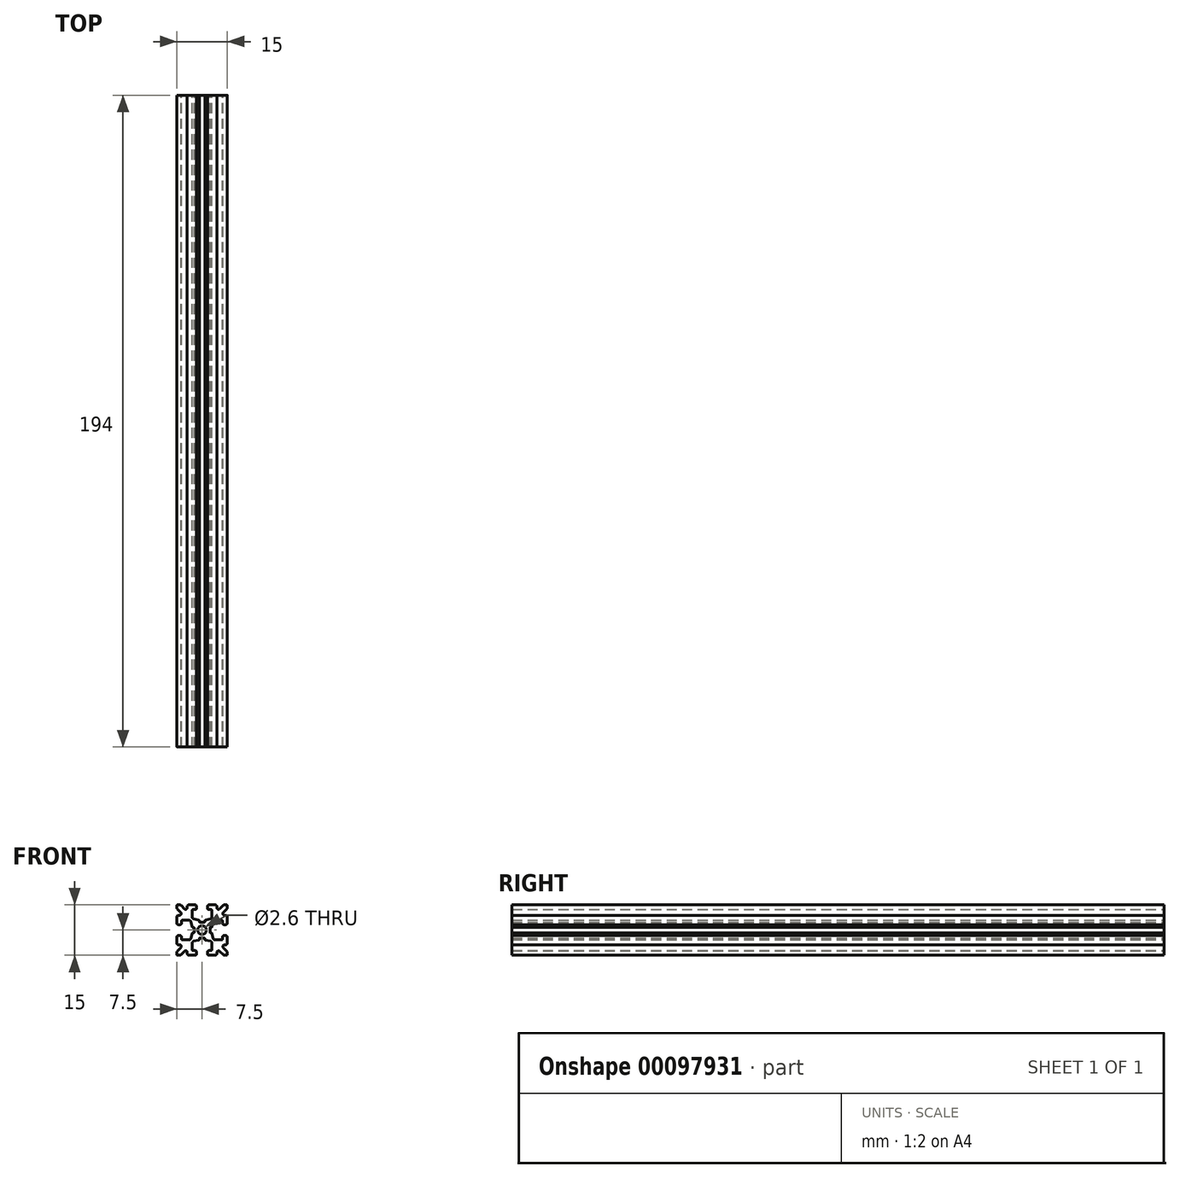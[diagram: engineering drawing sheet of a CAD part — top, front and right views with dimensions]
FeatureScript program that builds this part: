
annotation { "Feature Type Name" : "Feature", "Feature Type Description" : "" }
export const myFeature = defineFeature(function(context is Context, id is Id, definition is map)
    precondition{}
    {
        {
            var Q0;
            Q0=qCreatedBy(makeId("Front.planeOp"),FACE);
            var sketch = newSketch(context, id + "F0", { "sketchPlane" : qUnion([Q0])});
            skLineSegment(sketch, "E0.0.0", {"start": v(0.83, -2.55) * mm, "end": v(0.83, -2.77) * mm});
            skArc(sketch, "E0.0.1", {"start": v(0.83, -2.77) * mm, "mid": v(0.87, -2.9) * mm, "end": v(0.98, -2.97) * mm});
            skLineSegment(sketch, "E0.0.2", {"start": v(0.98, -2.97) * mm, "end": v(2.5, -3.31) * mm});
            skArc(sketch, "E0.0.3", {"start": v(2.5, -3.31) * mm, "mid": v(2.8, -3.49) * mm, "end": v(2.9, -3.8) * mm});
            skLineSegment(sketch, "E0.0.4", {"start": v(2.9, -3.8) * mm, "end": v(2.9, -5.9) * mm});
            skArc(sketch, "E0.0.5", {"start": v(2.9, -5.9) * mm, "mid": v(2.84, -6.04) * mm, "end": v(2.7, -6.1) * mm});
            skLineSegment(sketch, "E0.0.6", {"start": v(2.7, -6.1) * mm, "end": v(2.1, -6.1) * mm});
            skArc(sketch, "E0.0.7", {"start": v(2.1, -6.1) * mm, "mid": v(1.75, -6.25) * mm, "end": v(1.6, -6.6) * mm});
            skLineSegment(sketch, "E0.0.8", {"start": v(1.6, -6.6) * mm, "end": v(1.6, -7) * mm});
            skArc(sketch, "E0.0.9", {"start": v(1.6, -7) * mm, "mid": v(1.75, -7.35) * mm, "end": v(2.1, -7.5) * mm});
            skLineSegment(sketch, "E0.0.10", {"start": v(2.1, -7.5) * mm, "end": v(3.9, -7.5) * mm});
            skArc(sketch, "E0.0.11", {"start": v(3.9, -7.5) * mm, "mid": v(4.25, -7.35) * mm, "end": v(4.4, -7) * mm});
            skLineSegment(sketch, "E0.0.12", {"start": v(4.4, -7) * mm, "end": v(4.4, -6.67) * mm});
            skArc(sketch, "E0.0.13", {"start": v(4.4, -6.67) * mm, "mid": v(4.7, -6.2) * mm, "end": v(5.25, -6.31) * mm});
            skLineSegment(sketch, "E0.0.14", {"start": v(5.25, -6.31) * mm, "end": v(6.3, -7.35) * mm});
            skArc(sketch, "E0.0.15", {"start": v(6.3, -7.35) * mm, "mid": v(6.46, -7.46) * mm, "end": v(6.65, -7.5) * mm});
            skLineSegment(sketch, "E0.0.16", {"start": v(6.65, -7.5) * mm, "end": v(7.25, -7.5) * mm});
            skArc(sketch, "E0.0.17", {"start": v(7.25, -7.5) * mm, "mid": v(7.43, -7.43) * mm, "end": v(7.5, -7.25) * mm});
            skLineSegment(sketch, "E0.0.18", {"start": v(7.5, -7.25) * mm, "end": v(7.5, -6.65) * mm});
            skArc(sketch, "E0.0.19", {"start": v(7.5, -6.65) * mm, "mid": v(7.46, -6.46) * mm, "end": v(7.35, -6.3) * mm});
            skLineSegment(sketch, "E0.0.20", {"start": v(7.35, -6.3) * mm, "end": v(6.31, -5.25) * mm});
            skArc(sketch, "E0.0.21", {"start": v(6.31, -5.25) * mm, "mid": v(6.2, -4.7) * mm, "end": v(6.67, -4.4) * mm});
            skLineSegment(sketch, "E0.0.22", {"start": v(6.67, -4.4) * mm, "end": v(7, -4.4) * mm});
            skArc(sketch, "E0.0.23", {"start": v(7, -4.4) * mm, "mid": v(7.35, -4.25) * mm, "end": v(7.5, -3.9) * mm});
            skLineSegment(sketch, "E0.0.24", {"start": v(7.5, -3.9) * mm, "end": v(7.5, -2.1) * mm});
            skArc(sketch, "E0.0.25", {"start": v(7.5, -2.1) * mm, "mid": v(7.35, -1.75) * mm, "end": v(7, -1.6) * mm});
            skLineSegment(sketch, "E0.0.26", {"start": v(7, -1.6) * mm, "end": v(6.6, -1.6) * mm});
            skArc(sketch, "E0.0.27", {"start": v(6.6, -1.6) * mm, "mid": v(6.25, -1.75) * mm, "end": v(6.1, -2.1) * mm});
            skLineSegment(sketch, "E0.0.28", {"start": v(6.1, -2.1) * mm, "end": v(6.1, -2.7) * mm});
            skArc(sketch, "E0.0.29", {"start": v(6.1, -2.7) * mm, "mid": v(6.04, -2.84) * mm, "end": v(5.9, -2.9) * mm});
            skLineSegment(sketch, "E0.0.30", {"start": v(5.9, -2.9) * mm, "end": v(3.8, -2.9) * mm});
            skArc(sketch, "E0.0.31", {"start": v(3.8, -2.9) * mm, "mid": v(3.49, -2.8) * mm, "end": v(3.31, -2.5) * mm});
            skLineSegment(sketch, "E0.0.32", {"start": v(3.31, -2.5) * mm, "end": v(2.97, -0.98) * mm});
            skArc(sketch, "E0.0.33", {"start": v(2.97, -0.98) * mm, "mid": v(2.9, -0.87) * mm, "end": v(2.77, -0.83) * mm});
            skLineSegment(sketch, "E0.0.34", {"start": v(2.77, -0.83) * mm, "end": v(2.55, -0.83) * mm});
            skArc(sketch, "E0.0.35", {"start": v(2.55, -0.83) * mm, "mid": v(2.4, -0.77) * mm, "end": v(2.35, -0.63) * mm});
            skLineSegment(sketch, "E0.0.36", {"start": v(2.35, -0.63) * mm, "end": v(2.35, 0.63) * mm});
            skArc(sketch, "E0.0.37", {"start": v(2.35, 0.63) * mm, "mid": v(2.4, 0.77) * mm, "end": v(2.55, 0.83) * mm});
            skLineSegment(sketch, "E0.0.38", {"start": v(2.55, 0.83) * mm, "end": v(2.77, 0.83) * mm});
            skArc(sketch, "E0.0.39", {"start": v(2.77, 0.83) * mm, "mid": v(2.9, 0.87) * mm, "end": v(2.97, 0.98) * mm});
            skLineSegment(sketch, "E0.0.40", {"start": v(2.97, 0.98) * mm, "end": v(3.31, 2.5) * mm});
            skArc(sketch, "E0.0.41", {"start": v(3.31, 2.5) * mm, "mid": v(3.49, 2.8) * mm, "end": v(3.8, 2.9) * mm});
            skLineSegment(sketch, "E0.0.42", {"start": v(3.8, 2.9) * mm, "end": v(5.9, 2.9) * mm});
            skArc(sketch, "E0.0.43", {"start": v(5.9, 2.9) * mm, "mid": v(6.04, 2.84) * mm, "end": v(6.1, 2.7) * mm});
            skLineSegment(sketch, "E0.0.44", {"start": v(6.1, 2.7) * mm, "end": v(6.1, 2.1) * mm});
            skArc(sketch, "E0.0.45", {"start": v(6.1, 2.1) * mm, "mid": v(6.25, 1.75) * mm, "end": v(6.6, 1.6) * mm});
            skLineSegment(sketch, "E0.0.46", {"start": v(6.6, 1.6) * mm, "end": v(7, 1.6) * mm});
            skArc(sketch, "E0.0.47", {"start": v(7, 1.6) * mm, "mid": v(7.35, 1.75) * mm, "end": v(7.5, 2.1) * mm});
            skLineSegment(sketch, "E0.0.48", {"start": v(7.5, 2.1) * mm, "end": v(7.5, 3.9) * mm});
            skArc(sketch, "E0.0.49", {"start": v(7.5, 3.9) * mm, "mid": v(7.35, 4.25) * mm, "end": v(7, 4.4) * mm});
            skLineSegment(sketch, "E0.0.50", {"start": v(7, 4.4) * mm, "end": v(6.67, 4.4) * mm});
            skArc(sketch, "E0.0.51", {"start": v(6.67, 4.4) * mm, "mid": v(6.2, 4.7) * mm, "end": v(6.31, 5.25) * mm});
            skLineSegment(sketch, "E0.0.52", {"start": v(6.31, 5.25) * mm, "end": v(7.35, 6.3) * mm});
            skArc(sketch, "E0.0.53", {"start": v(7.35, 6.3) * mm, "mid": v(7.46, 6.46) * mm, "end": v(7.5, 6.65) * mm});
            skLineSegment(sketch, "E0.0.54", {"start": v(7.5, 6.65) * mm, "end": v(7.5, 7.25) * mm});
            skArc(sketch, "E0.0.55", {"start": v(7.5, 7.25) * mm, "mid": v(7.43, 7.43) * mm, "end": v(7.25, 7.5) * mm});
            skLineSegment(sketch, "E0.0.56", {"start": v(7.25, 7.5) * mm, "end": v(6.65, 7.5) * mm});
            skArc(sketch, "E0.0.57", {"start": v(6.65, 7.5) * mm, "mid": v(6.46, 7.46) * mm, "end": v(6.3, 7.35) * mm});
            skLineSegment(sketch, "E0.0.58", {"start": v(6.3, 7.35) * mm, "end": v(5.25, 6.31) * mm});
            skArc(sketch, "E0.0.59", {"start": v(5.25, 6.31) * mm, "mid": v(4.7, 6.2) * mm, "end": v(4.4, 6.67) * mm});
            skLineSegment(sketch, "E0.0.60", {"start": v(4.4, 6.67) * mm, "end": v(4.4, 7) * mm});
            skArc(sketch, "E0.0.61", {"start": v(4.4, 7) * mm, "mid": v(4.25, 7.35) * mm, "end": v(3.9, 7.5) * mm});
            skLineSegment(sketch, "E0.0.62", {"start": v(3.9, 7.5) * mm, "end": v(2.1, 7.5) * mm});
            skArc(sketch, "E0.0.63", {"start": v(2.1, 7.5) * mm, "mid": v(1.75, 7.35) * mm, "end": v(1.6, 7) * mm});
            skLineSegment(sketch, "E0.0.64", {"start": v(1.6, 7) * mm, "end": v(1.6, 6.6) * mm});
            skArc(sketch, "E0.0.65", {"start": v(1.6, 6.6) * mm, "mid": v(1.75, 6.25) * mm, "end": v(2.1, 6.1) * mm});
            skLineSegment(sketch, "E0.0.66", {"start": v(2.1, 6.1) * mm, "end": v(2.7, 6.1) * mm});
            skArc(sketch, "E0.0.67", {"start": v(2.7, 6.1) * mm, "mid": v(2.84, 6.04) * mm, "end": v(2.9, 5.9) * mm});
            skLineSegment(sketch, "E0.0.68", {"start": v(2.9, 5.9) * mm, "end": v(2.9, 3.8) * mm});
            skArc(sketch, "E0.0.69", {"start": v(2.9, 3.8) * mm, "mid": v(2.8, 3.49) * mm, "end": v(2.5, 3.31) * mm});
            skLineSegment(sketch, "E0.0.70", {"start": v(2.5, 3.31) * mm, "end": v(0.98, 2.97) * mm});
            skArc(sketch, "E0.0.71", {"start": v(0.98, 2.97) * mm, "mid": v(0.87, 2.9) * mm, "end": v(0.83, 2.77) * mm});
            skLineSegment(sketch, "E0.0.72", {"start": v(0.83, 2.77) * mm, "end": v(0.83, 2.55) * mm});
            skArc(sketch, "E0.0.73", {"start": v(0.83, 2.55) * mm, "mid": v(0.77, 2.4) * mm, "end": v(0.63, 2.35) * mm});
            skLineSegment(sketch, "E0.0.74", {"start": v(0.63, 2.35) * mm, "end": v(-0.63, 2.35) * mm});
            skArc(sketch, "E0.0.75", {"start": v(-0.63, 2.35) * mm, "mid": v(-0.77, 2.4) * mm, "end": v(-0.83, 2.55) * mm});
            skLineSegment(sketch, "E0.0.76", {"start": v(-0.83, 2.55) * mm, "end": v(-0.83, 2.77) * mm});
            skArc(sketch, "E0.0.77", {"start": v(-0.83, 2.77) * mm, "mid": v(-0.87, 2.9) * mm, "end": v(-0.98, 2.97) * mm});
            skLineSegment(sketch, "E0.0.78", {"start": v(-0.98, 2.97) * mm, "end": v(-2.5, 3.31) * mm});
            skArc(sketch, "E0.0.79", {"start": v(-2.5, 3.31) * mm, "mid": v(-2.8, 3.49) * mm, "end": v(-2.9, 3.8) * mm});
            skLineSegment(sketch, "E0.0.80", {"start": v(-2.9, 3.8) * mm, "end": v(-2.9, 5.9) * mm});
            skArc(sketch, "E0.0.81", {"start": v(-2.9, 5.9) * mm, "mid": v(-2.84, 6.04) * mm, "end": v(-2.7, 6.1) * mm});
            skLineSegment(sketch, "E0.0.82", {"start": v(-2.7, 6.1) * mm, "end": v(-2.1, 6.1) * mm});
            skArc(sketch, "E0.0.83", {"start": v(-2.1, 6.1) * mm, "mid": v(-1.75, 6.25) * mm, "end": v(-1.6, 6.6) * mm});
            skLineSegment(sketch, "E0.0.84", {"start": v(-1.6, 6.6) * mm, "end": v(-1.6, 7) * mm});
            skArc(sketch, "E0.0.85", {"start": v(-1.6, 7) * mm, "mid": v(-1.75, 7.35) * mm, "end": v(-2.1, 7.5) * mm});
            skLineSegment(sketch, "E0.0.86", {"start": v(-2.1, 7.5) * mm, "end": v(-3.9, 7.5) * mm});
            skArc(sketch, "E0.0.87", {"start": v(-3.9, 7.5) * mm, "mid": v(-4.25, 7.35) * mm, "end": v(-4.4, 7) * mm});
            skLineSegment(sketch, "E0.0.88", {"start": v(-4.4, 7) * mm, "end": v(-4.4, 6.67) * mm});
            skArc(sketch, "E0.0.89", {"start": v(-4.4, 6.67) * mm, "mid": v(-4.7, 6.2) * mm, "end": v(-5.25, 6.31) * mm});
            skLineSegment(sketch, "E0.0.90", {"start": v(-5.25, 6.31) * mm, "end": v(-6.3, 7.35) * mm});
            skArc(sketch, "E0.0.91", {"start": v(-6.3, 7.35) * mm, "mid": v(-6.46, 7.46) * mm, "end": v(-6.65, 7.5) * mm});
            skLineSegment(sketch, "E0.0.92", {"start": v(-6.65, 7.5) * mm, "end": v(-7.25, 7.5) * mm});
            skArc(sketch, "E0.0.93", {"start": v(-7.25, 7.5) * mm, "mid": v(-7.43, 7.43) * mm, "end": v(-7.5, 7.25) * mm});
            skLineSegment(sketch, "E0.0.94", {"start": v(-7.5, 7.25) * mm, "end": v(-7.5, 6.65) * mm});
            skArc(sketch, "E0.0.95", {"start": v(-7.5, 6.65) * mm, "mid": v(-7.46, 6.46) * mm, "end": v(-7.35, 6.3) * mm});
            skLineSegment(sketch, "E0.0.96", {"start": v(-7.35, 6.3) * mm, "end": v(-6.31, 5.25) * mm});
            skArc(sketch, "E0.0.97", {"start": v(-6.31, 5.25) * mm, "mid": v(-6.2, 4.7) * mm, "end": v(-6.67, 4.4) * mm});
            skLineSegment(sketch, "E0.0.98", {"start": v(-6.67, 4.4) * mm, "end": v(-7, 4.4) * mm});
            skArc(sketch, "E0.0.99", {"start": v(-7, 4.4) * mm, "mid": v(-7.35, 4.25) * mm, "end": v(-7.5, 3.9) * mm});
            skLineSegment(sketch, "E0.0.100", {"start": v(-7.5, 3.9) * mm, "end": v(-7.5, 2.1) * mm});
            skArc(sketch, "E0.0.101", {"start": v(-7.5, 2.1) * mm, "mid": v(-7.35, 1.75) * mm, "end": v(-7, 1.6) * mm});
            skLineSegment(sketch, "E0.0.102", {"start": v(-7, 1.6) * mm, "end": v(-6.6, 1.6) * mm});
            skArc(sketch, "E0.0.103", {"start": v(-6.6, 1.6) * mm, "mid": v(-6.25, 1.75) * mm, "end": v(-6.1, 2.1) * mm});
            skLineSegment(sketch, "E0.0.104", {"start": v(-6.1, 2.1) * mm, "end": v(-6.1, 2.7) * mm});
            skArc(sketch, "E0.0.105", {"start": v(-6.1, 2.7) * mm, "mid": v(-6.04, 2.84) * mm, "end": v(-5.9, 2.9) * mm});
            skLineSegment(sketch, "E0.0.106", {"start": v(-5.9, 2.9) * mm, "end": v(-3.8, 2.9) * mm});
            skArc(sketch, "E0.0.107", {"start": v(-3.8, 2.9) * mm, "mid": v(-3.49, 2.8) * mm, "end": v(-3.31, 2.5) * mm});
            skLineSegment(sketch, "E0.0.108", {"start": v(-3.31, 2.5) * mm, "end": v(-2.97, 0.98) * mm});
            skArc(sketch, "E0.0.109", {"start": v(-2.97, 0.98) * mm, "mid": v(-2.9, 0.87) * mm, "end": v(-2.77, 0.83) * mm});
            skLineSegment(sketch, "E0.0.110", {"start": v(-2.77, 0.83) * mm, "end": v(-2.55, 0.83) * mm});
            skArc(sketch, "E0.0.111", {"start": v(-2.55, 0.83) * mm, "mid": v(-2.4, 0.77) * mm, "end": v(-2.35, 0.63) * mm});
            skLineSegment(sketch, "E0.0.112", {"start": v(-2.35, 0.63) * mm, "end": v(-2.35, -0.63) * mm});
            skArc(sketch, "E0.0.113", {"start": v(-2.35, -0.63) * mm, "mid": v(-2.4, -0.77) * mm, "end": v(-2.55, -0.83) * mm});
            skLineSegment(sketch, "E0.0.114", {"start": v(-2.55, -0.83) * mm, "end": v(-2.77, -0.83) * mm});
            skArc(sketch, "E0.0.115", {"start": v(-2.77, -0.83) * mm, "mid": v(-2.9, -0.87) * mm, "end": v(-2.97, -0.98) * mm});
            skLineSegment(sketch, "E0.0.116", {"start": v(-2.97, -0.98) * mm, "end": v(-3.31, -2.5) * mm});
            skArc(sketch, "E0.0.117", {"start": v(-3.31, -2.5) * mm, "mid": v(-3.49, -2.8) * mm, "end": v(-3.8, -2.9) * mm});
            skLineSegment(sketch, "E0.0.118", {"start": v(-3.8, -2.9) * mm, "end": v(-5.9, -2.9) * mm});
            skArc(sketch, "E0.0.119", {"start": v(-5.9, -2.9) * mm, "mid": v(-6.04, -2.84) * mm, "end": v(-6.1, -2.7) * mm});
            skLineSegment(sketch, "E0.0.120", {"start": v(-6.1, -2.7) * mm, "end": v(-6.1, -2.1) * mm});
            skArc(sketch, "E0.0.121", {"start": v(-6.1, -2.1) * mm, "mid": v(-6.25, -1.75) * mm, "end": v(-6.6, -1.6) * mm});
            skLineSegment(sketch, "E0.0.122", {"start": v(-6.6, -1.6) * mm, "end": v(-7, -1.6) * mm});
            skArc(sketch, "E0.0.123", {"start": v(-7, -1.6) * mm, "mid": v(-7.35, -1.75) * mm, "end": v(-7.5, -2.1) * mm});
            skLineSegment(sketch, "E0.0.124", {"start": v(-7.5, -2.1) * mm, "end": v(-7.5, -3.9) * mm});
            skArc(sketch, "E0.0.125", {"start": v(-7.5, -3.9) * mm, "mid": v(-7.35, -4.25) * mm, "end": v(-7, -4.4) * mm});
            skLineSegment(sketch, "E0.0.126", {"start": v(-7, -4.4) * mm, "end": v(-6.67, -4.4) * mm});
            skArc(sketch, "E0.0.127", {"start": v(-6.67, -4.4) * mm, "mid": v(-6.2, -4.7) * mm, "end": v(-6.31, -5.25) * mm});
            skLineSegment(sketch, "E0.0.128", {"start": v(-6.31, -5.25) * mm, "end": v(-7.35, -6.3) * mm});
            skArc(sketch, "E0.0.129", {"start": v(-7.35, -6.3) * mm, "mid": v(-7.46, -6.46) * mm, "end": v(-7.5, -6.65) * mm});
            skLineSegment(sketch, "E0.0.130", {"start": v(-7.5, -6.65) * mm, "end": v(-7.5, -7.25) * mm});
            skArc(sketch, "E0.0.131", {"start": v(-7.5, -7.25) * mm, "mid": v(-7.43, -7.43) * mm, "end": v(-7.25, -7.5) * mm});
            skLineSegment(sketch, "E0.0.132", {"start": v(-7.25, -7.5) * mm, "end": v(-6.65, -7.5) * mm});
            skArc(sketch, "E0.0.133", {"start": v(-6.65, -7.5) * mm, "mid": v(-6.46, -7.46) * mm, "end": v(-6.3, -7.35) * mm});
            skLineSegment(sketch, "E0.0.134", {"start": v(-6.3, -7.35) * mm, "end": v(-5.25, -6.31) * mm});
            skArc(sketch, "E0.0.135", {"start": v(-5.25, -6.31) * mm, "mid": v(-4.7, -6.2) * mm, "end": v(-4.4, -6.67) * mm});
            skLineSegment(sketch, "E0.0.136", {"start": v(-4.4, -6.67) * mm, "end": v(-4.4, -7) * mm});
            skArc(sketch, "E0.0.137", {"start": v(-4.4, -7) * mm, "mid": v(-4.25, -7.35) * mm, "end": v(-3.9, -7.5) * mm});
            skLineSegment(sketch, "E0.0.138", {"start": v(-3.9, -7.5) * mm, "end": v(-2.1, -7.5) * mm});
            skArc(sketch, "E0.0.139", {"start": v(-2.1, -7.5) * mm, "mid": v(-1.75, -7.35) * mm, "end": v(-1.6, -7) * mm});
            skLineSegment(sketch, "E0.0.140", {"start": v(-1.6, -7) * mm, "end": v(-1.6, -6.6) * mm});
            skArc(sketch, "E0.0.141", {"start": v(-1.6, -6.6) * mm, "mid": v(-1.75, -6.25) * mm, "end": v(-2.1, -6.1) * mm});
            skLineSegment(sketch, "E0.0.142", {"start": v(-2.1, -6.1) * mm, "end": v(-2.7, -6.1) * mm});
            skArc(sketch, "E0.0.143", {"start": v(-2.7, -6.1) * mm, "mid": v(-2.84, -6.04) * mm, "end": v(-2.9, -5.9) * mm});
            skLineSegment(sketch, "E0.0.144", {"start": v(-2.9, -5.9) * mm, "end": v(-2.9, -3.8) * mm});
            skArc(sketch, "E0.0.145", {"start": v(-2.9, -3.8) * mm, "mid": v(-2.8, -3.49) * mm, "end": v(-2.5, -3.31) * mm});
            skLineSegment(sketch, "E0.0.146", {"start": v(-2.5, -3.31) * mm, "end": v(-0.98, -2.97) * mm});
            skArc(sketch, "E0.0.147", {"start": v(-0.98, -2.97) * mm, "mid": v(-0.87, -2.9) * mm, "end": v(-0.83, -2.77) * mm});
            skLineSegment(sketch, "E0.0.148", {"start": v(-0.83, -2.77) * mm, "end": v(-0.83, -2.55) * mm});
            skArc(sketch, "E0.0.149", {"start": v(-0.83, -2.55) * mm, "mid": v(-0.77, -2.4) * mm, "end": v(-0.63, -2.35) * mm});
            skLineSegment(sketch, "E0.0.150", {"start": v(-0.63, -2.35) * mm, "end": v(0.63, -2.35) * mm});
            skArc(sketch, "E0.0.151", {"start": v(0.63, -2.35) * mm, "mid": v(0.77, -2.4) * mm, "end": v(0.83, -2.55) * mm});
            skPoint(sketch, "E1", {"position": v(0, 0) * mm});
            skPoint(sketch, "E1.positionSnap0", {"position": v(0, 2.35) * mm});
            skPoint(sketch, "E1.positionSnap1", {"position": v(2.35, 0) * mm});
            skCircle(sketch, "E2", {"center": v(0, 0) * mm, "radius": 1.3 * mm});
            skSolve(sketch);
        }
        {
            var Q0;
            Q0=makeQuery(id+"F0.imprint","IMPRINT",FACE,{"disambiguationData":[TD([[makeQuery(id+"F0.imprint","IMPRINT",EDGE,{"derivedFrom":sQuery(id+"F0.wireOp",EDGE,"E0.0.0")}),1.0]])]});
            extrude(context, id + "F1", {"entities" : qUnion([Q0]), "endBound" : BoundingType.SYMMETRIC, "depth" : 194 * mm});
        }
    });
